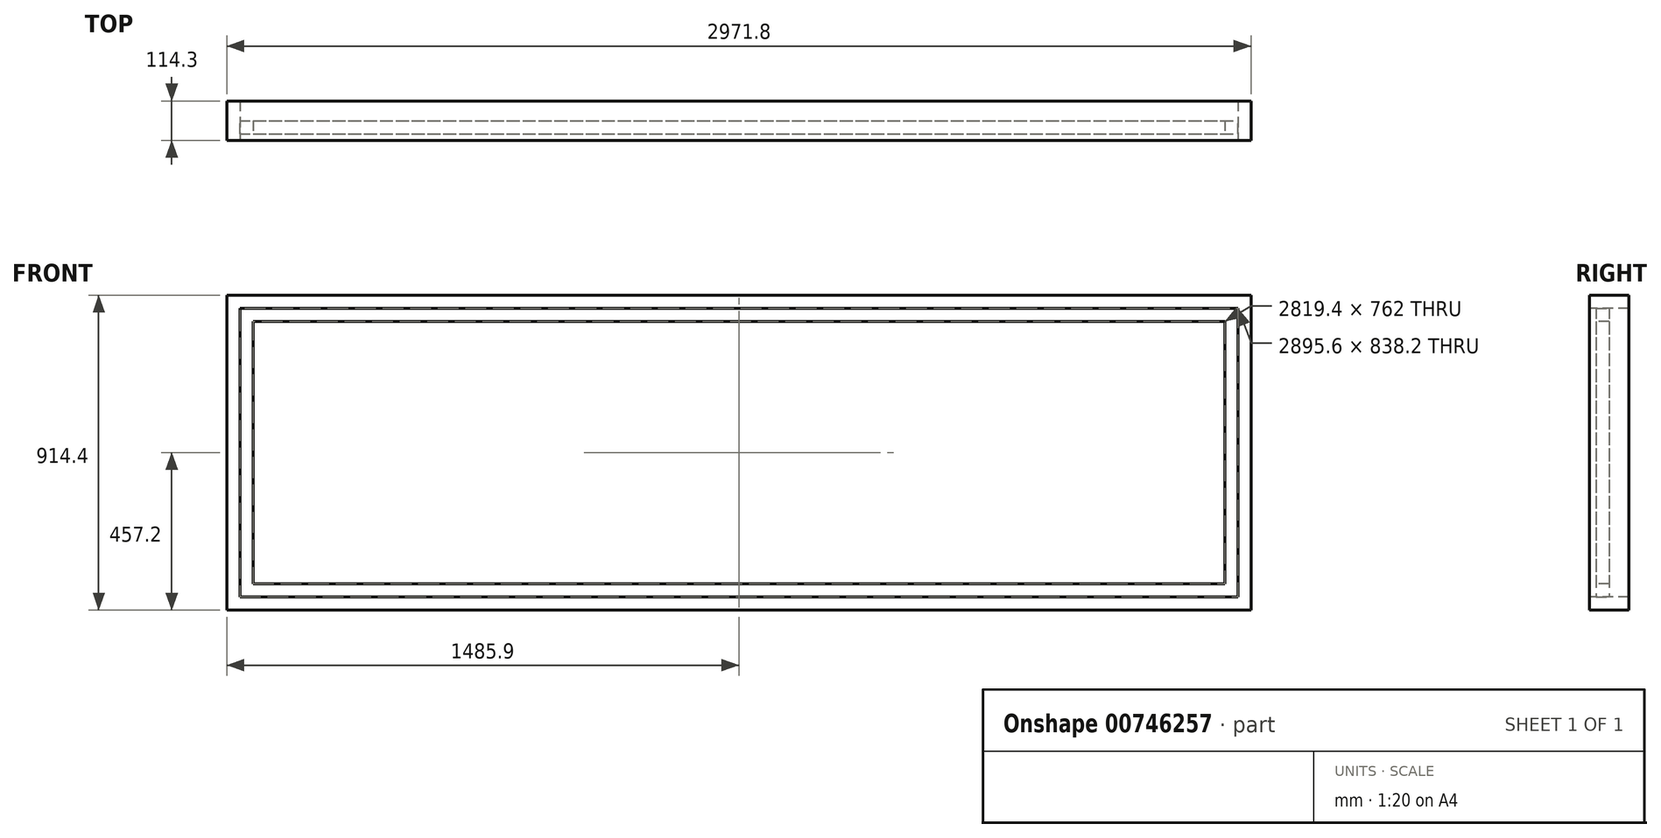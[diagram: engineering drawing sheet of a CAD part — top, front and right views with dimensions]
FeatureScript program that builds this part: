
annotation { "Feature Type Name" : "Feature", "Feature Type Description" : "" }
export const myFeature = defineFeature(function(context is Context, id is Id, definition is map)
    precondition{}
    {
        {
            var Q0;
            Q0=qCreatedBy(makeId("Front.planeOp"),FACE);
            var sketch = newSketch(context, id + "F0", { "sketchPlane" : qUnion([Q0])});
            skLineSegment(sketch, "E0.bottom", {"start": v(-1485.9, 457.2) * mm, "end": v(1485.9, 457.2) * mm});
            skLineSegment(sketch, "E0.top", {"start": v(-1485.9, -457.2) * mm, "end": v(1485.9, -457.2) * mm});
            skLineSegment(sketch, "E0.left", {"start": v(-1485.9, 457.2) * mm, "end": v(-1485.9, -457.2) * mm});
            skLineSegment(sketch, "E0.right", {"start": v(1485.9, 457.2) * mm, "end": v(1485.9, -457.2) * mm});
            skLineSegment(sketch, "E1", {"start": v(0, 457.2) * mm, "end": v(0, 0) * mm, "construction": true});
            skLineSegment(sketch, "E2", {"start": v(0, 0) * mm, "end": v(-1485.9, 0) * mm, "construction": true});
            skSolve(sketch);
        }
        {
            var Q0;
            Q0=makeQuery(id+"F0.imprint","IMPRINT",FACE,{"disambiguationData":[TD([[makeQuery(id+"F0.imprint","IMPRINT",EDGE,{"derivedFrom":sQuery(id+"F0.wireOp",EDGE,"E0.bottom")}),-1.0]])]});
            extrude(context, id + "F1", {"entities" : qUnion([Q0]), "endBound" : BoundingType.SYMMETRIC, "depth" : 114.3 * mm, "offsetDistance" : 25.4 * mm});
        }
        {
            var Q0;
            Q0=makeQuery(id+"F1.opExtrude","CAP_FACE",FACE,{"disambiguationData":[OSD([sQuery(id+"F0.wireOp",EDGE,"E0.bottom"),sQuery(id+"F0.wireOp",EDGE,"E0.top"),sQuery(id+"F0.wireOp",EDGE,"E0.left"),sQuery(id+"F0.wireOp",EDGE,"E0.right")])],"isStart":false});
            var sketch = newSketch(context, id + "F2", { "sketchPlane" : qUnion([Q0])});
            skLineSegment(sketch, "E3.bottom", {"start": v(-1447.8, 419.1) * mm, "end": v(1447.8, 419.1) * mm});
            skLineSegment(sketch, "E3.top", {"start": v(-1447.8, -419.1) * mm, "end": v(1447.8, -419.1) * mm});
            skLineSegment(sketch, "E3.left", {"start": v(-1447.8, 419.1) * mm, "end": v(-1447.8, -419.1) * mm});
            skLineSegment(sketch, "E3.right", {"start": v(1447.8, 419.1) * mm, "end": v(1447.8, -419.1) * mm});
            skSolve(sketch);
        }
        {
            var Q0;
            Q0=makeQuery(id+"F2.imprint","IMPRINT",FACE,{"disambiguationData":[TD([[makeQuery(id+"F2.imprint","IMPRINT",EDGE,{"derivedFrom":sQuery(id+"F2.wireOp",EDGE,"E3.bottom")}),-1.0]])]});
            extrude(context, id + "F3", {"entities" : qUnion([Q0]), "operationType" : NewBodyOperationType.REMOVE, "endBound" : BoundingType.THROUGH_ALL, "oppositeDirection" : true, "depth" : 25.4 * mm, "offsetDistance" : 25.4 * mm});
        }
        {
            var Q0;
            Q0=qCreatedBy(makeId("Front.planeOp"),FACE);
            var sketch = newSketch(context, id + "F4", { "sketchPlane" : qUnion([Q0])});
            skLineSegment(sketch, "E4.bottom", {"start": v(-1447.8, 419.1) * mm, "end": v(1447.8, 419.1) * mm});
            skLineSegment(sketch, "E4.top", {"start": v(-1447.8, -419.1) * mm, "end": v(1447.8, -419.1) * mm});
            skLineSegment(sketch, "E4.left", {"start": v(-1447.8, 419.1) * mm, "end": v(-1447.8, -419.1) * mm});
            skLineSegment(sketch, "E4.right", {"start": v(1447.8, 419.1) * mm, "end": v(1447.8, -419.1) * mm});
            skSolve(sketch);
        }
        {
            var Q0;
            Q0=makeQuery(id+"F4.imprint","IMPRINT",FACE,{"disambiguationData":[TD([[makeQuery(id+"F4.imprint","IMPRINT",EDGE,{"derivedFrom":sQuery(id+"F4.wireOp",EDGE,"E4.bottom")}),-1.0]])]});
            extrude(context, id + "F5", {"entities" : qUnion([Q0]), "depth" : 38.1 * mm, "offsetDistance" : 25.4 * mm});
        }
        {
            var Q0;
            Q0=makeQuery(id+"F5.opExtrude","CAP_FACE",FACE,{"disambiguationData":[OSD([sQuery(id+"F4.wireOp",EDGE,"E4.bottom"),sQuery(id+"F4.wireOp",EDGE,"E4.top"),sQuery(id+"F4.wireOp",EDGE,"E4.left"),sQuery(id+"F4.wireOp",EDGE,"E4.right")])],"isStart":false});
            var sketch = newSketch(context, id + "F6", { "sketchPlane" : qUnion([Q0])});
            skLineSegment(sketch, "E5.bottom", {"start": v(-1409.7, 381) * mm, "end": v(1409.7, 381) * mm});
            skLineSegment(sketch, "E5.top", {"start": v(-1409.7, -381) * mm, "end": v(1409.7, -381) * mm});
            skLineSegment(sketch, "E5.left", {"start": v(-1409.7, 381) * mm, "end": v(-1409.7, -381) * mm});
            skLineSegment(sketch, "E5.right", {"start": v(1409.7, 381) * mm, "end": v(1409.7, -381) * mm});
            skSolve(sketch);
        }
        {
            var Q0;
            Q0=qSketchRegion(id+"F6",true);
            extrude(context, id + "F7", {"entities" : qUnion([Q0]), "operationType" : NewBodyOperationType.REMOVE, "endBound" : BoundingType.THROUGH_ALL, "oppositeDirection" : true, "depth" : 25.4 * mm, "offsetDistance" : 25.4 * mm});
        }
        {
            var Q0;
            Q0=qCreatedBy(makeId("Front.planeOp"),FACE);
            var sketch = newSketch(context, id + "F8", { "sketchPlane" : qUnion([Q0])});
            skLineSegment(sketch, "E6.bottom", {"start": v(-19.05, 419.1) * mm, "end": v(1447.8, 419.1) * mm});
            skLineSegment(sketch, "E6.top", {"start": v(-19.05, -419.1) * mm, "end": v(1447.8, -419.1) * mm});
            skLineSegment(sketch, "E6.left", {"start": v(-19.05, 419.1) * mm, "end": v(-19.05, -419.1) * mm});
            skLineSegment(sketch, "E6.right", {"start": v(1447.8, 419.1) * mm, "end": v(1447.8, -419.1) * mm});
            skSolve(sketch);
        }
        {
            var Q0;
            Q0=qSketchRegion(id+"F8",true);
            extrude(context, id + "F9", {"entities" : qUnion([Q0]), "oppositeDirection" : true, "depth" : 38.1 * mm, "offsetDistance" : 25.4 * mm});
        }
        {
            var Q0;
            Q0=makeQuery(id+"F9.opExtrude","CAP_FACE",FACE,{"disambiguationData":[OSD([sQuery(id+"F8.wireOp",EDGE,"E6.bottom"),sQuery(id+"F8.wireOp",EDGE,"E6.top"),sQuery(id+"F8.wireOp",EDGE,"E6.left"),sQuery(id+"F8.wireOp",EDGE,"E6.right")])],"isStart":true});
            var sketch = newSketch(context, id + "F10", { "sketchPlane" : qUnion([Q0])});
            skLineSegment(sketch, "E7.bottom", {"start": v(1409.7, 381) * mm, "end": v(1447.8, 381) * mm});
            skLineSegment(sketch, "E7.top", {"start": v(1409.7, -381) * mm, "end": v(1447.8, -381) * mm});
            skLineSegment(sketch, "E7.left", {"start": v(1447.8, 381) * mm, "end": v(1447.8, -381) * mm});
            skLineSegment(sketch, "E7.right", {"start": v(1409.7, 381) * mm, "end": v(1409.7, -381) * mm});
            skSolve(sketch);
        }
        {
            var Q0;
            Q0=qSketchRegion(id+"F10",true);
            extrude(context, id + "F11", {"entities" : qUnion([Q0]), "operationType" : NewBodyOperationType.REMOVE, "endBound" : BoundingType.THROUGH_ALL, "oppositeDirection" : true, "depth" : 25.4 * mm, "offsetDistance" : 25.4 * mm});
        }
        {
            var Q0;
            Q0=makeQuery(id+"F9.opExtrude","SWEPT_BODY",BODY,{"disambiguationData":[OSD([sQuery(id+"F8.wireOp",EDGE,"E6.bottom"),sQuery(id+"F8.wireOp",EDGE,"E6.top"),sQuery(id+"F8.wireOp",EDGE,"E6.left"),sQuery(id+"F8.wireOp",EDGE,"E6.right")])]});
            deleteBodies(context, id + "F12", {"entities" : qUnion([Q0])});
        }
    });
